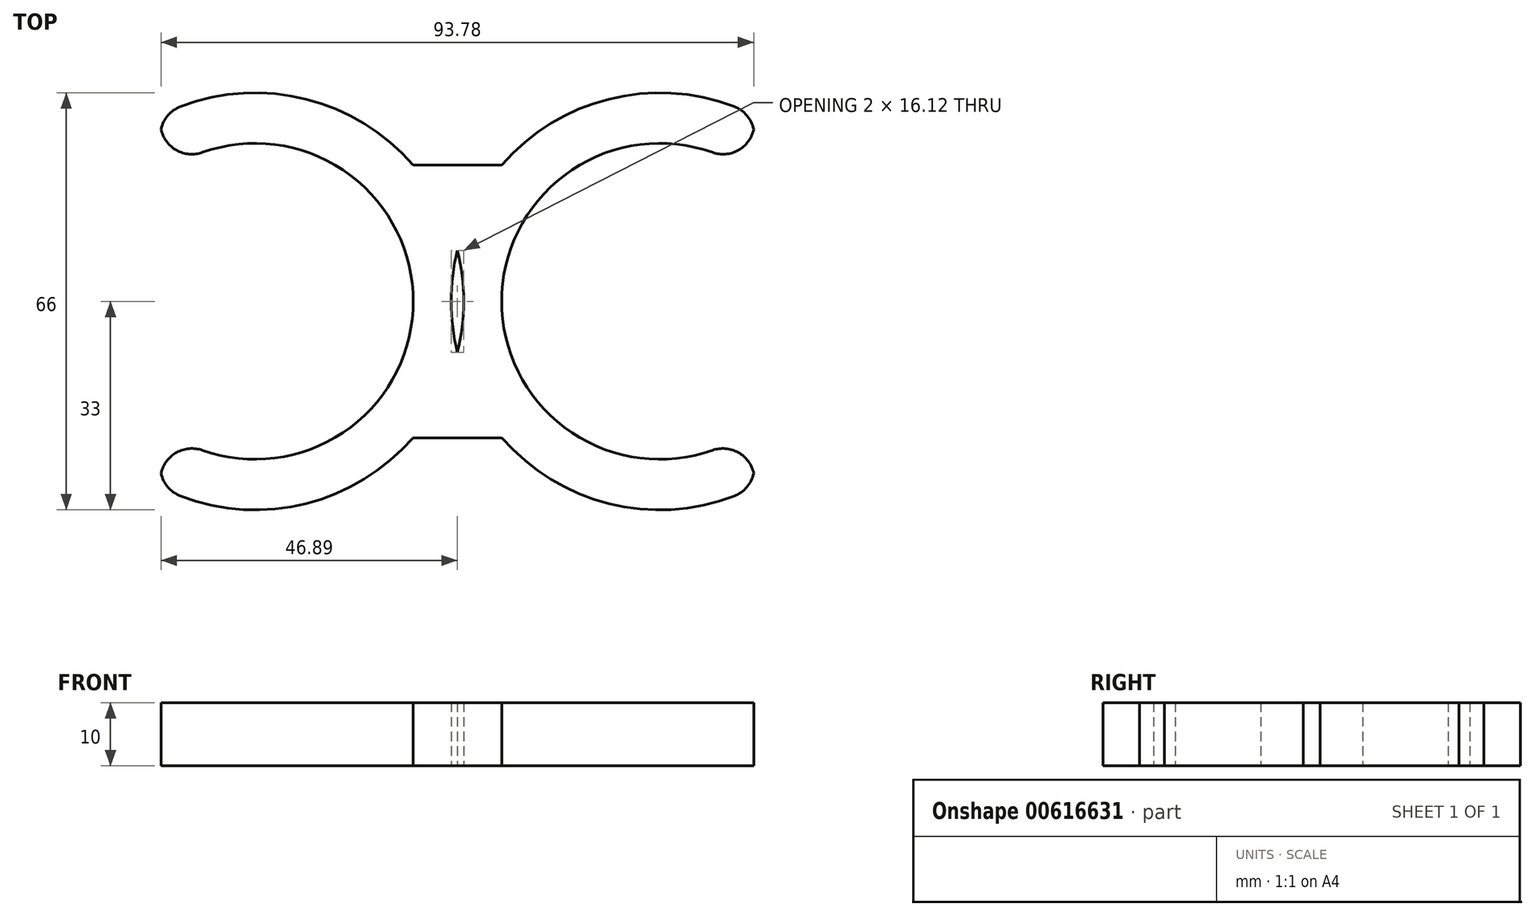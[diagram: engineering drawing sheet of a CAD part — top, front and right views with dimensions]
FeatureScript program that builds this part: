
annotation { "Feature Type Name" : "Feature", "Feature Type Description" : "" }
export const myFeature = defineFeature(function(context is Context, id is Id, definition is map)
    precondition{}
    {
        {
            var Q0;
            Q0=qCreatedBy(makeId("Top.planeOp"),FACE);
            var sketch = newSketch(context, id + "F0", { "sketchPlane" : qUnion([Q0])});
            skArc(sketch, "E0", {"start": v(-47, -20) * mm, "mid": v(-7, 0) * mm, "end": v(-47, 20) * mm});
            skArc(sketch, "E1", {"start": v(-47, -29.4) * mm, "mid": v(1, 0) * mm, "end": v(-47, 29.4) * mm});
            skLineSegment(sketch, "E2", {"start": v(-47, 29.4) * mm, "end": v(-47, 20) * mm});
            skLineSegment(sketch, "E3.trimOffspring", {"start": v(-47, -20) * mm, "end": v(-47, -29.4) * mm});
            skArc(sketch, "E4.MirrorCS", {"start": v(47, -20) * mm, "mid": v(7, 0) * mm, "end": v(47, 20) * mm});
            skArc(sketch, "E5.MirrorCS", {"start": v(47, -29.4) * mm, "mid": v(-1, 0) * mm, "end": v(47, 29.4) * mm});
            skLineSegment(sketch, "E6.MirrorCS", {"start": v(47, 29.4) * mm, "end": v(47, 20) * mm});
            skLineSegment(sketch, "E7.MirrorCS", {"start": v(47, -20) * mm, "end": v(47, -29.4) * mm});
            skLineSegment(sketch, "E8.bottom", {"start": v(-7.04, 21.58) * mm, "end": v(7.04, 21.58) * mm});
            skLineSegment(sketch, "E8.top", {"start": v(-7.04, -21.58) * mm, "end": v(7.04, -21.58) * mm});
            skLineSegment(sketch, "E8.left", {"start": v(-7.04, 21.58) * mm, "end": v(-7.04, -21.58) * mm});
            skLineSegment(sketch, "E8.right", {"start": v(7.04, 21.58) * mm, "end": v(7.04, -21.58) * mm});
            skPoint(sketch, "E8.middle", {"position": v(0, 0) * mm});
            skSolve(sketch);
        }
        {
            var Q0;
            Q0 = qSketchRegion(id + "F0", true);
            var Q1;
            {var subQ0=sQuery(id+"F0.wireOp",EDGE,"E5.MirrorCS");var subQ1=sQuery(id+"F0.wireOp",EDGE,"E1");var subQ2=makeQuery(id+"F0.imprint","INTERSECT",VERTEX,{"disambiguationData":[OD(0.0)],"derivedFrom":[subQ1,subQ0]});Q1=makeQuery(id+"F0.imprint","IMPRINT",FACE,{"disambiguationData":[TD([[makeQuery(id+"F0.imprint","IMPRINT",EDGE,{"disambiguationData":[TD([[subQ2,-1.0]])],"derivedFrom":subQ1}),1.0]])]});}
            extrude(context, id + "F1", {"entities" : qUnion([Q0, Q1]), "depth" : 5 * mm, "offsetDistance" : 25 * mm, "hasSecondDirection" : true, "secondDirectionOppositeDirection" : true, "secondDirectionDepth" : 5 * mm});
        }
        {
            var Q0;
            Q0=makeQuery(id+"F1.opExtrude","SWEPT_EDGE",EDGE,{"disambiguationData":[OSD([sQuery(id+"F0.wireOp",EDGE,"E0"),sQuery(id+"F0.wireOp",EDGE,"E2")])]});
            var Q1;
            Q1=makeQuery(id+"F1.opExtrude","SWEPT_EDGE",EDGE,{"disambiguationData":[OSD([sQuery(id+"F0.wireOp",EDGE,"E1"),sQuery(id+"F0.wireOp",EDGE,"E3.trimOffspring")])]});
            var Q2;
            Q2=makeQuery(id+"F1.opExtrude","SWEPT_EDGE",EDGE,{"disambiguationData":[OSD([sQuery(id+"F0.wireOp",EDGE,"E0"),sQuery(id+"F0.wireOp",EDGE,"E3.trimOffspring")])]});
            var Q3;
            Q3=makeQuery(id+"F1.opExtrude","SWEPT_EDGE",EDGE,{"disambiguationData":[OSD([sQuery(id+"F0.wireOp",EDGE,"E1"),sQuery(id+"F0.wireOp",EDGE,"E2")])]});
            var Q4;
            Q4=makeQuery(id+"F1.opExtrude","SWEPT_EDGE",EDGE,{"disambiguationData":[OSD([sQuery(id+"F0.wireOp",EDGE,"E5.MirrorCS"),sQuery(id+"F0.wireOp",EDGE,"E7.MirrorCS")])]});
            var Q5;
            Q5=makeQuery(id+"F1.opExtrude","SWEPT_EDGE",EDGE,{"disambiguationData":[OSD([sQuery(id+"F0.wireOp",EDGE,"E4.MirrorCS"),sQuery(id+"F0.wireOp",EDGE,"E7.MirrorCS")])]});
            var Q6;
            Q6=makeQuery(id+"F1.opExtrude","SWEPT_EDGE",EDGE,{"disambiguationData":[OSD([sQuery(id+"F0.wireOp",EDGE,"E4.MirrorCS"),sQuery(id+"F0.wireOp",EDGE,"E6.MirrorCS")])]});
            var Q7;
            Q7=makeQuery(id+"F1.opExtrude","SWEPT_EDGE",EDGE,{"disambiguationData":[OSD([sQuery(id+"F0.wireOp",EDGE,"E5.MirrorCS"),sQuery(id+"F0.wireOp",EDGE,"E6.MirrorCS")])]});
            fillet(context, id + "F2", {"entities" : qUnion([Q0, Q1, Q2, Q3, Q4, Q5, Q6, Q7]), "radius" : 5 * mm, "tangentPropagation" : true, "allowEdgeOverflow" : false});
        }
    });
